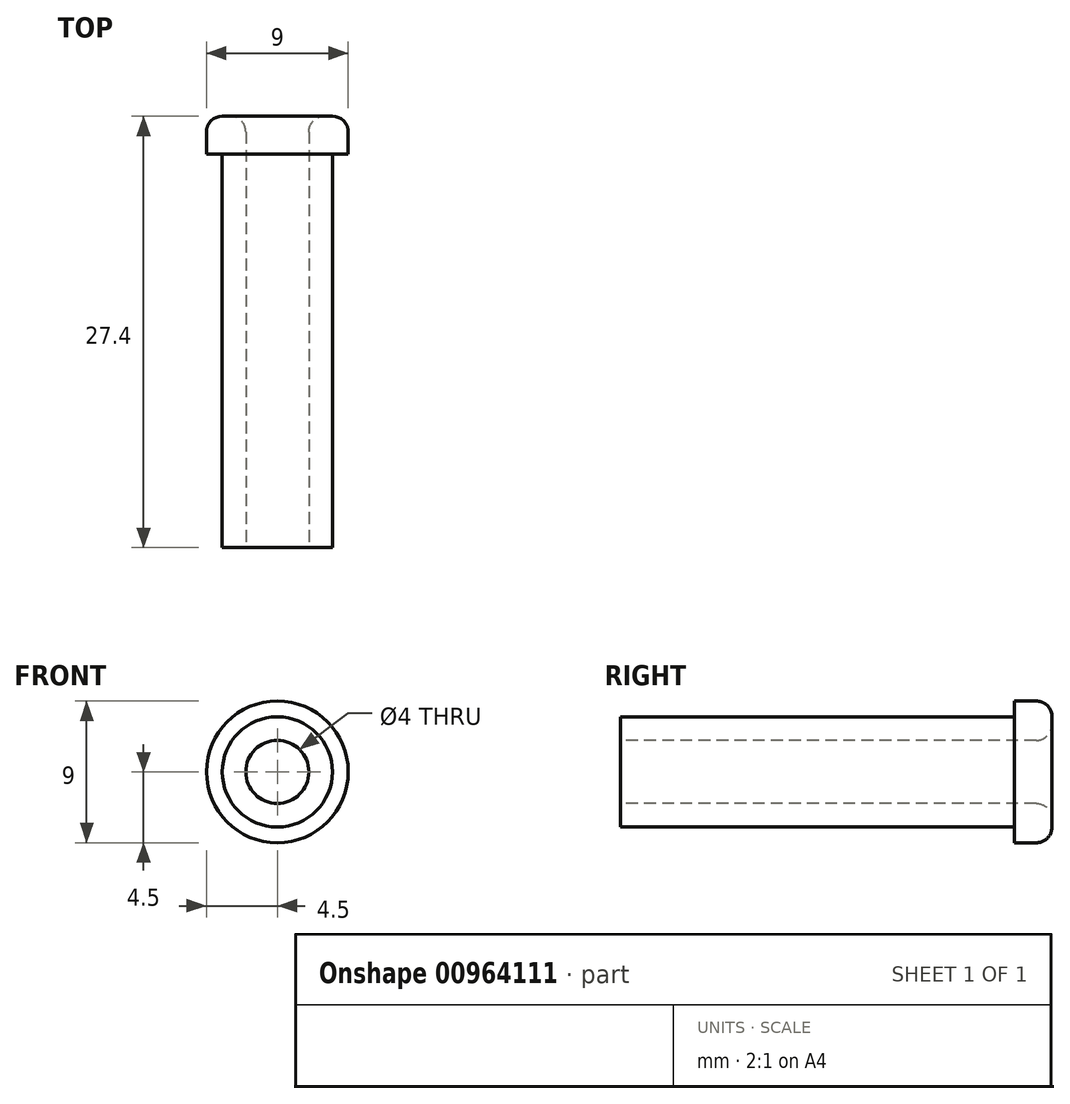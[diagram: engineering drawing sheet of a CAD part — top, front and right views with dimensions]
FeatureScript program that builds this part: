
annotation { "Feature Type Name" : "Feature", "Feature Type Description" : "" }
export const myFeature = defineFeature(function(context is Context, id is Id, definition is map)
    precondition{}
    {
        {
            var Q0;
            Q0=qCreatedBy(makeId("Top.planeOp"),FACE);
            var sketch = newSketch(context, id + "F0", { "sketchPlane" : qUnion([Q0])});
            skLineSegment(sketch, "E0", {"start": v(2, 0) * mm, "end": v(2, 27.4) * mm});
            skLineSegment(sketch, "E1", {"start": v(2, 27.4) * mm, "end": v(4.5, 27.4) * mm});
            skLineSegment(sketch, "E2", {"start": v(4.5, 27.4) * mm, "end": v(4.5, 25) * mm});
            skLineSegment(sketch, "E3", {"start": v(4.5, 25) * mm, "end": v(3.5, 25) * mm});
            skLineSegment(sketch, "E4", {"start": v(3.5, 25) * mm, "end": v(3.5, 0) * mm});
            skLineSegment(sketch, "E5", {"start": v(3.5, 0) * mm, "end": v(2, 0) * mm});
            skLineSegment(sketch, "E6", {"start": v(0, 0) * mm, "end": v(0, 28) * mm, "construction": true});
            skSolve(sketch);
        }
        {
            var Q0;
            Q0=makeQuery(id+"F0.imprint","IMPRINT",FACE,{"disambiguationData":[TD([[makeQuery(id+"F0.imprint","IMPRINT",EDGE,{"derivedFrom":sQuery(id+"F0.wireOp",EDGE,"E0")}),-1.0]])]});
            var Q1;
            Q1=sQuery(id+"F0.wireOp",EDGE,"E6");
            revolve(context, id + "F1", {"surfaceOperationType" : NewSurfaceOperationType.NEW, "entities" : qUnion([Q0]), "axis" : qUnion([Q1]), "revolveType" : RevolveType.FULL});
        }
        {
            var Q0;
            Q0=makeQuery(id+"F1.opRevolve","SWEPT_FACE",FACE,{"disambiguationData":[OSD([sQuery(id+"F0.wireOp",EDGE,"E1")])]});
            fillet(context, id + "F2", {"entities" : qUnion([Q0]), "radius" : 1 * mm, "allowEdgeOverflow" : false});
        }
    });
